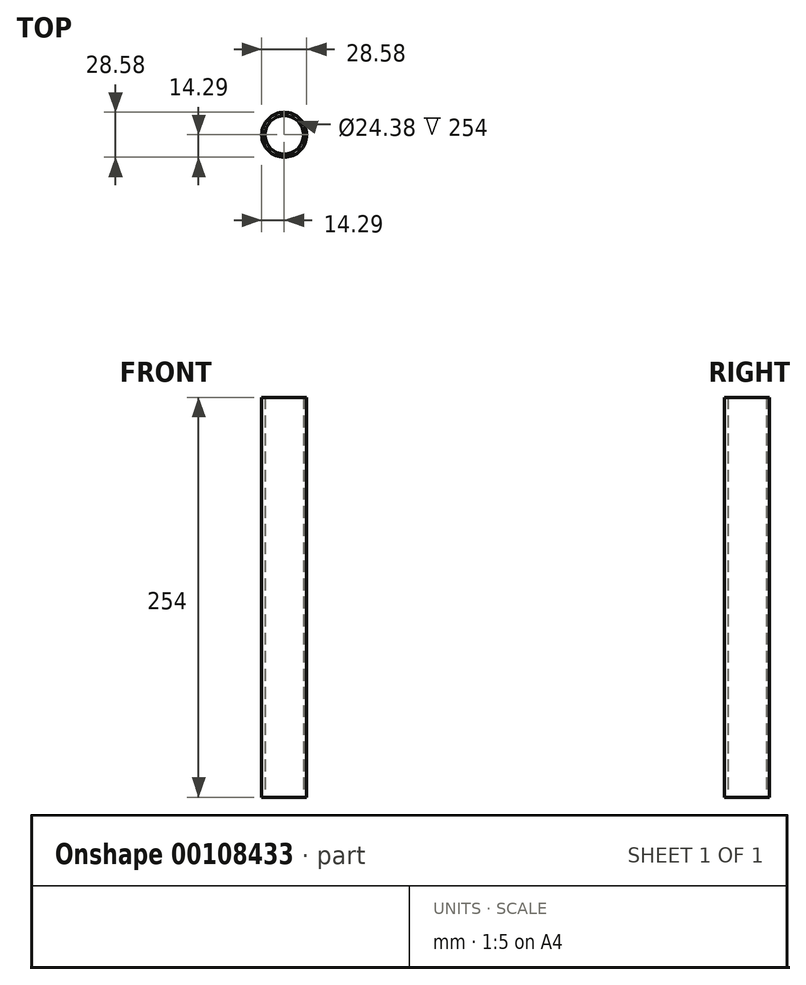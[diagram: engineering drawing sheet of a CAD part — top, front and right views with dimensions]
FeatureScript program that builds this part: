
annotation { "Feature Type Name" : "Feature", "Feature Type Description" : "" }
export const myFeature = defineFeature(function(context is Context, id is Id, definition is map)
    precondition{}
    {
        {
            var Q0;
            Q0=qCreatedBy(makeId("Top.planeOp"),FACE);
            var sketch = newSketch(context, id + "F0", { "sketchPlane" : qUnion([Q0])});
            skCircle(sketch, "E0", {"center": v(0, 0) * mm, "radius": 14.29 * mm});
            skCircle(sketch, "E1", {"center": v(0, 0) * mm, "radius": 12.19 * mm});
            skSolve(sketch);
        }
        {
            var Q0;
            Q0=makeQuery(id+"F0.imprint","IMPRINT",FACE,{"disambiguationData":[TD([[makeQuery(id+"F0.imprint","IMPRINT",EDGE,{"derivedFrom":sQuery(id+"F0.wireOp",EDGE,"E0")}),1.0]])]});
            extrude(context, id + "F1", {"entities" : qUnion([Q0]), "depth" : 254 * mm, "symmetric" : true});
        }
    });
